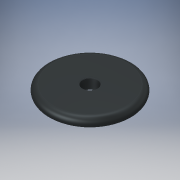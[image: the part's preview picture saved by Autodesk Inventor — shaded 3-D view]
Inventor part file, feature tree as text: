
AUTODESK INVENTOR PART (.ipt)
format: ipt  version: 2019 (Build 230136000, 136)  size: 125,952 bytes
history: native  units: in
note: dims shown in document units (in); Inventor stores cm internally (conversion verified against a paired STEP export)
features: extrude x1, fillet x1, chamfer x1, sketch x1
ambient origin geometry x8: Origin, YZ Plane, XZ Plane, XY Plane, X Axis, Y Axis, Z Axis, Center Point
bodies: Solid1 (feature_tree)
feature tree (4):
  extrude  "Extrusion1"  Depth=0.375in
  fillet  "Fillet1"  Radius=0.75in
  chamfer  "Chamfer1"  Distance=0.375in
  sketch  "Sketch1"  dims[d0=6.1in d1=1.1in d2=0.75in d3=0.0in d4=0.375in d5=0.025in d6=0.125in d7=45.0deg]
